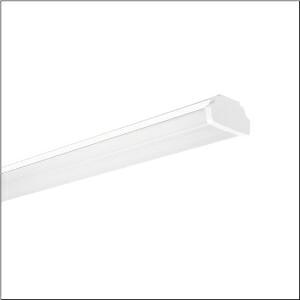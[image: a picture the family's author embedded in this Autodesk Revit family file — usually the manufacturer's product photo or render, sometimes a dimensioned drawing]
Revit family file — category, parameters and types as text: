
# Revit family: modario_r__31_ho_53bm811m1v4120_5d14
name_source: partatom
category: Lighting Fixtures
units: mm (PartAtom-declared; Revit-internal decimal feet)

## family parameters
Cut with Voids When Loaded = No
Host = Face
Light Source = No
Part Type = Normal
Room Calculation Point = No
Round Connector Dimension = Use Diameter
Shared = No

## types (1)
- --- (1 x LED, 12380 lm, 77.3 W, 4000K)
    Apparent Load = 77 VA
    CIE Flux Codes = 52 78 94 90 100
    Color Rendering = 80
    Color Temperature = 4000K
    Default Elevation = 1800 mm
    Description = Modario® 31 HO, luminaire insert, of sheet steel, coil coated, white, length: 1.495mm, width: 81mm, height: 82mm, 5x system unit, system units: 299mm, LED rated luminous flux: 12.380lm, light colour: 840, control gear: ON/OFF Multilumen, control gear: ECG Multilumen, with plug, 3-pole, with phase selection, mains connection: 220..240V, AC, 50/60Hz, rated input power: 77W, through-wiring accessed according to module size, primary optical cover: cover, of PMMA, light emission: direct distribution, primary light characteristic: symmetric, protection rating (complete): IP20, protection rating (LED compartment): IP50, insulation class (complete): insulation class I (protective earthing), certification: CE, ENEC, VDE, UKCA, impact resistance: IK03, permissible ambient temperature for indoor applications: -35..+35°C, corresponds to IFS (International Featured Standards) requirements for safety and quality in the food industry, reducing of maximum allowable ambient temperature of 5°C with ceiling mounting, packaging unit: 1 piece
    Height = 92 mm
    Lamp = 1 x LED
    Lamp Light Flux = 12380 lm
    Lamp Power = 77.3 W
    Lamp count = 1
    Length = 1495 mm
    Luminous efficacy = 160 lm/W
    Manufacturer = Siteco
    ModVariant = No
    Model = 53BM811M1V4120
    Mounting Place = Ceiling
    Mounting Type = Pendant
    Number of Poles = 1
    OnlyDefault = Yes
    Power Factor = 1
    Product Name = Modario® 31 HO
    Product group = luminaire insert
    ProductGroupID = 901
    Protection Class = Protection class I
    Protection Degree = IP 20
    RLX_Detail_Level = 1
    RLX_Emergency_Light_Flux = 0 lm
    RLX_Emergency_Type = 0
    RLX_Emergency_Type_DB = No
    RlxData = <blob elided: 39913 chars, md5=e60e2c37>
    Socket = socket
    Standby Power = 0 W
    System Light Flux = 12380 lm
    System Power = 77 W
    Type Comments = factory setting: luminous flux: 100 % | (A | C | E) | 173 mA
    Type Image = l_1300283.jpg
    URL = http://relux.com
    VarID = @adj_134643
    Voltage = 0 V
    Weight = 0.00 kg
    Width = 81 mm

## geometry (parser evidence)
native form markers: Blend x4, Sweep x11
no freeform markers — native parametric forms only
